# Revit family: D100_GRYFIT CX-4S + SMN, Fire damper
name_source: partatom
category: Duct Accessories
revit_build: Autodesk Revit 2018 (Build: 20190510_1515(x64)
units: mm (PartAtom-declared; Revit-internal decimal feet)

## family parameters
Always vertical = Yes
Cut with Voids When Loaded = No
OmniClass Number = 23.75.70.11.14.14
OmniClass Title = Dampers for Air Ductwork
Part Type = Damper
Round Connector Dimension = Use Diameter
Shared = No
Work Plane-Based = No

## types (1)
- GRYFIT CX-4S + SMN, male collar, D=100 + WT72C + SRV_G + SRV_H + TG, D=100. P=150
    95°C = 72°C
    Actuator type. = FDG-WT-5
    Actuator voltage. = 24/48 V AC/DC
    Connector. = male collar
    Damper Length = 150 mm
    Damper Material = <By Category>
    Diameter (D). = 100
    Double Beginning and End (2WKKP) = None
    EMS module = No
    EPDM Gaskets = Yes
    Empty49 = 0
    Fire resistance class. = EI 60 (ve-ho-i↔o) S
    Geometry = GRYFIT CX-4S + SMN, male collar, D=100 + WT72C + SRV_G + SRV_H + TG, D=100. P=150
    Half Damper Length = 75 mm
    Length (M). = 0
    Length (N). = 92.5
    Length (O). = 0
    Length (P). = 150
    Mounting hole diameter (Dr). = 110
    Type. = GRYFIT CX-4S + SMN
    anglXY1 = 180.00°
    anglXY2 = 0.00°
    anglZ1 = 0.00°
    anglZ2 = 0.00°
    diamcon1 = 100 mm
    diamcon2 = 100 mm
    lengX1 = 0 mm  [stored 0 ft]
    lengX2 = 35 mm  [stored 0.114829 ft]
    lengXY1 = 600 mm
    lengXY2 = 600 mm
    lengXYZ1 = 500 mm  [stored 1.64042 ft]
    lengXYZ2 = 500 mm  [stored 1.64042 ft]
    lengY1 = 0 mm  [stored 0 ft]
    lengY2 = 0 mm  [stored 0 ft]
    lengZ1 = 0 mm  [stored 0 ft]
    lengZ2 = 0 mm  [stored 0 ft]

note: [stored X ft] marks values corroborated as IEEE doubles in the binary element streams (Revit-internal decimal feet)

## geometry (parser evidence)
native form markers: Sweep x3
no freeform markers — native parametric forms only
